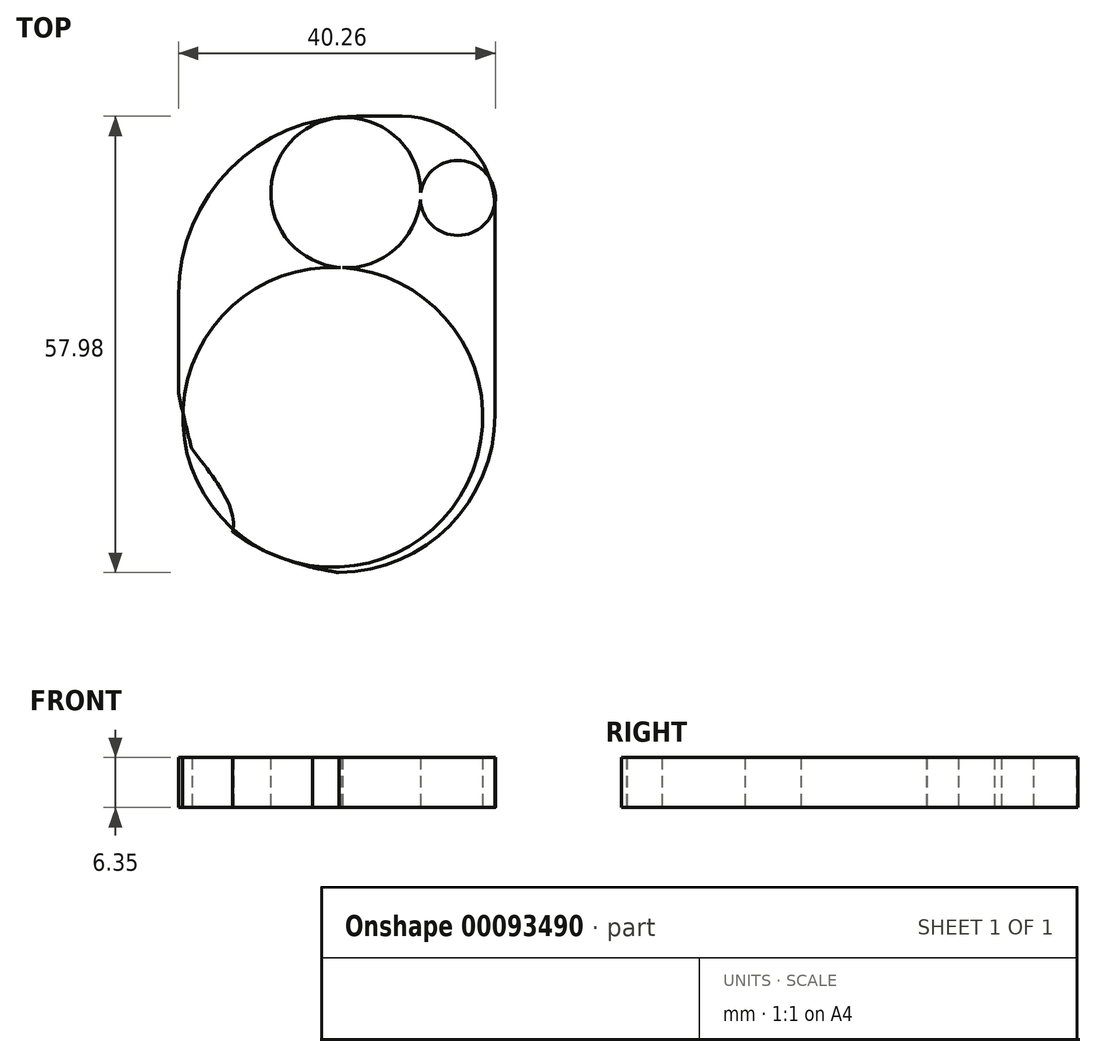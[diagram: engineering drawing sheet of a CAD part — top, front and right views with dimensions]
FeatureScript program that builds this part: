
annotation { "Feature Type Name" : "Feature", "Feature Type Description" : "" }
export const myFeature = defineFeature(function(context is Context, id is Id, definition is map)
    precondition{}
    {
        {
            var Q0;
            Q0=qCreatedBy(makeId("Top.planeOp"),FACE);
            var sketch = newSketch(context, id + "F0", { "sketchPlane" : qUnion([Q0])});
            skCircle(sketch, "E0", {"center": v(-20.6, -7.27) * mm, "radius": 19.05 * mm});
            skCircle(sketch, "E1", {"center": v(-18.95, 21.25) * mm, "radius": 9.53 * mm});
            skPoint(sketch, "E1.first.point", {"position": v(-19.39, 11.74) * mm});
            skPoint(sketch, "E1.second.point", {"position": v(-18.84, 30.78) * mm});
            skPoint(sketch, "E1.third.point", {"position": v(-24.96, 28.65) * mm});
            skCircle(sketch, "E2", {"center": v(-4.71, 20.58) * mm, "radius": 4.76 * mm});
            skPoint(sketch, "E2.first.point", {"position": v(-9.43, 21.25) * mm});
            skPoint(sketch, "E2.second.point", {"position": v(0, 21.25) * mm});
            skPoint(sketch, "E2.third.point", {"position": v(-3.29, 25.12) * mm});
            skSolve(sketch);
        }
        {
            var Q0;
            Q0=qCreatedBy(makeId("Top.planeOp"),FACE);
            var sketch = newSketch(context, id + "F1", { "sketchPlane" : qUnion([Q0])});
            skLineSegment(sketch, "E3", {"start": v(-19.8, -27.02) * mm, "end": v(-20.06, -27.02) * mm});
            skLineSegment(sketch, "E4.top", {"start": v(-17.6, 30.96) * mm, "end": v(-11.78, 30.96) * mm});
            skLineSegment(sketch, "E4.left", {"start": v(-40.2, -4.18) * mm, "end": v(-40.2, 8.36) * mm});
            skLineSegment(sketch, "E4.right", {"start": v(0, -6.96) * mm, "end": v(0, 19.18) * mm});
            skPoint(sketch, "E5.orphan", {"position": v(-40.2, -45.96) * mm});
            skPoint(sketch, "E6.visualSharp", {"position": v(0, -27.02) * mm});
            skArc(sketch, "E6.filletArc", {"start": v(-20.06, -27.02) * mm, "mid": v(-5.87, -21.15) * mm, "end": v(0, -6.96) * mm});
            skPoint(sketch, "E7.visualSharp", {"position": v(-40.2, 30.96) * mm});
            skArc(sketch, "E7.filletArc", {"start": v(-17.6, 30.96) * mm, "mid": v(-33.59, 24.34) * mm, "end": v(-40.2, 8.36) * mm});
            skPoint(sketch, "E8.visualSharp", {"position": v(0, 30.96) * mm});
            skArc(sketch, "E8.filletArc", {"start": v(0, 19.18) * mm, "mid": v(-3.45, 27.51) * mm, "end": v(-11.78, 30.96) * mm});
            skFitSpline(sketch, "E9", {"points": [v(-40.2, -4.18) * mm, v(-33.32, -21.84) * mm, v(-19.8, -27.02) * mm], "startDerivative": vector(8.62, -38.95) * mm, "endDerivative": vector(32.73, -6) * mm});
            skFitSpline(sketch, "E10", {"points": [v(-38.68, -11.1) * mm, v(-33.32, -21.84) * mm, v(-43.82, -29.38) * mm], "startDerivative": vector(18.64, -23.6) * mm, "endDerivative": vector(-28.63, -13) * mm});
            skLineSegment(sketch, "E11.trimOffspring", {"start": v(-33.32, -21.84) * mm, "end": v(-33.32, -21.84) * mm});
            skFitSpline(sketch, "E12", {"points": [v(-40.2, -4.18) * mm, v(-33.32, -21.84) * mm, v(-20.06, -27.02) * mm, v(-19.8, -27.02) * mm], "startDerivative": vector(5.23, -40.32) * mm, "endDerivative": vector(2.34, 0.42) * mm});
            skSolve(sketch);
        }
        {
            var Q0;
            Q0=sQuery(id+"F0.wireOp",EDGE,"E1");
            extrude(context, id + "F2", {"bodyType" : ToolBodyType.SURFACE, "surfaceEntities" : qUnion([Q0]), "depth" : 6.35 * mm});
        }
        {
            var Q0;
            {var subQ0=sQuery(id+"F0.wireOp",EDGE,"E1");var subQ1=sQuery(id+"F0.wireOp",EDGE,"E0");var subQ2=makeQuery(id+"F0.imprint","INTERSECT",VERTEX,{"disambiguationData":[OD(0.0)],"derivedFrom":[subQ1,subQ0]});Q0=makeQuery(id+"F0.imprint","IMPRINT",FACE,{"disambiguationData":[TD([[makeQuery(id+"F0.imprint","IMPRINT",EDGE,{"disambiguationData":[TD([[subQ2,-1.0]])],"derivedFrom":subQ1}),1.0]])]});}
            var Q1;
            {var subQ0=sQuery(id+"F0.wireOp",EDGE,"E2");var subQ1=sQuery(id+"F0.wireOp",EDGE,"E1");var subQ2=makeQuery(id+"F0.imprint","INTERSECT",VERTEX,{"disambiguationData":[OD(0.0)],"derivedFrom":[subQ1,subQ0]});Q1=makeQuery(id+"F0.imprint","IMPRINT",FACE,{"disambiguationData":[TD([[makeQuery(id+"F0.imprint","IMPRINT",EDGE,{"disambiguationData":[TD([[subQ2,1.0]])],"derivedFrom":subQ1}),-1.0]])]});}
            var Q2;
            {var subQ0=sQuery(id+"F0.wireOp",EDGE,"E1");var subQ1=sQuery(id+"F0.wireOp",EDGE,"E0");var subQ2=makeQuery(id+"F0.imprint","INTERSECT",VERTEX,{"disambiguationData":[OD(0.0)],"derivedFrom":[subQ1,subQ0]});Q2=makeQuery(id+"F0.imprint","IMPRINT",FACE,{"disambiguationData":[TD([[makeQuery(id+"F0.imprint","IMPRINT",EDGE,{"disambiguationData":[TD([[subQ2,1.0]])],"derivedFrom":subQ1}),-1.0]])]});}
            var Q3;
            {var subQ0=sQuery(id+"F0.wireOp",EDGE,"E1");var subQ1=sQuery(id+"F0.wireOp",EDGE,"E0");var subQ2=makeQuery(id+"F0.imprint","INTERSECT",VERTEX,{"disambiguationData":[OD(0.0)],"derivedFrom":[subQ1,subQ0]});Q3=makeQuery(id+"F0.imprint","IMPRINT",FACE,{"disambiguationData":[TD([[makeQuery(id+"F0.imprint","IMPRINT",EDGE,{"disambiguationData":[TD([[subQ2,1.0]])],"derivedFrom":subQ1}),1.0]])]});}
            var Q4;
            {var subQ0=sQuery(id+"F0.wireOp",EDGE,"E2");var subQ1=sQuery(id+"F0.wireOp",EDGE,"E1");var subQ2=makeQuery(id+"F0.imprint","INTERSECT",VERTEX,{"disambiguationData":[OD(0.0)],"derivedFrom":[subQ1,subQ0]});Q4=makeQuery(id+"F0.imprint","IMPRINT",FACE,{"disambiguationData":[TD([[makeQuery(id+"F0.imprint","IMPRINT",EDGE,{"disambiguationData":[TD([[subQ2,1.0]])],"derivedFrom":subQ1}),1.0]])]});}
            var Q5;
            Q5=makeQuery(id+"F1.imprint","IMPRINT",FACE,{"disambiguationData":[TD([[makeQuery(id+"F1.imprint","IMPRINT",EDGE,{"derivedFrom":sQuery(id+"F1.wireOp",EDGE,"E4.top")}),-1.0]])]});
            extrude(context, id + "F3", {"entities" : qUnion([Q0, Q1, Q2, Q3, Q4, Q5]), "depth" : 6.35 * mm});
        }
    });
